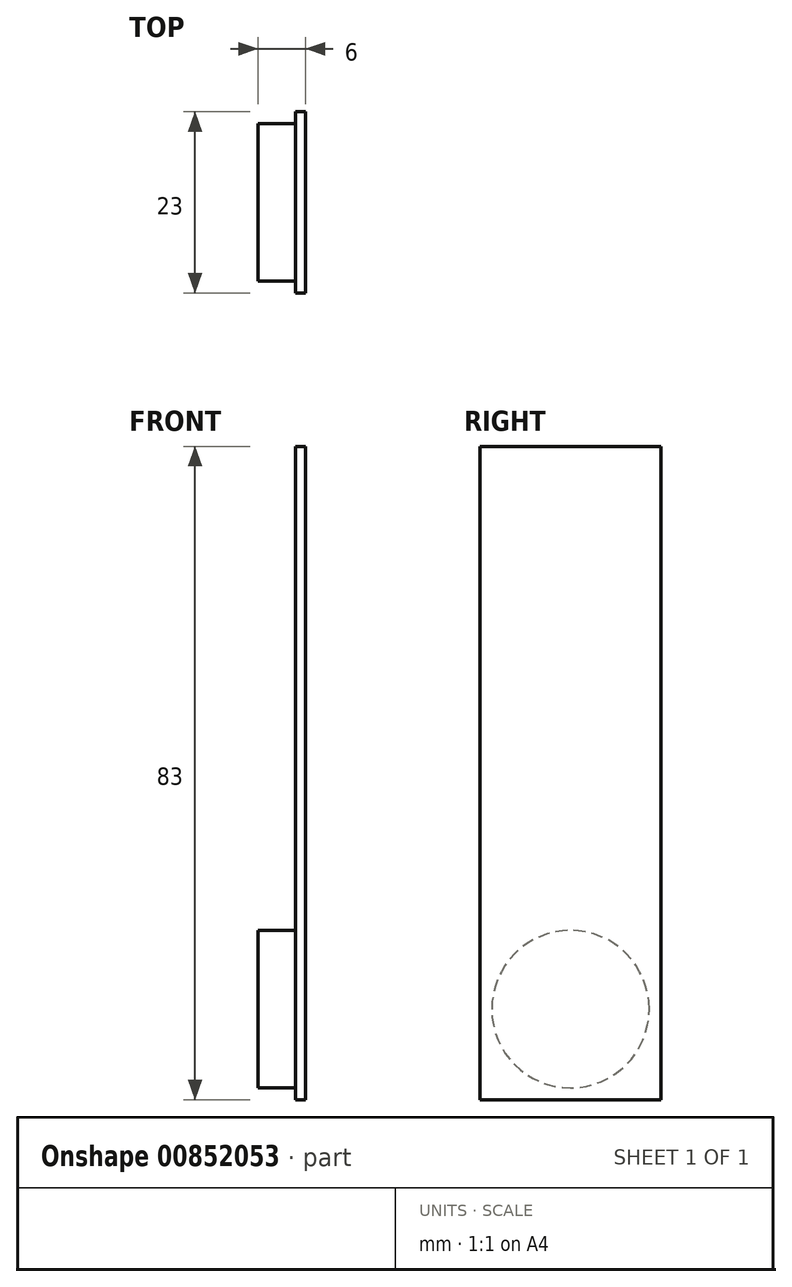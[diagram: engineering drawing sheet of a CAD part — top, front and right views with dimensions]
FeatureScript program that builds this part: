
annotation { "Feature Type Name" : "Feature", "Feature Type Description" : "" }
export const myFeature = defineFeature(function(context is Context, id is Id, definition is map)
    precondition{}
    {
        {
            var Q0;
            Q0=qCreatedBy(makeId("Top.planeOp"),FACE);
            var sketch = newSketch(context, id + "F0", { "sketchPlane" : qUnion([Q0])});
            skLineSegment(sketch, "E0.bottom", {"start": v(-9.84, -11.5) * mm, "end": v(-3.84, -11.5) * mm});
            skLineSegment(sketch, "E0.top", {"start": v(-9.84, 11.5) * mm, "end": v(-3.84, 11.5) * mm});
            skLineSegment(sketch, "E0.left", {"start": v(-9.84, -11.5) * mm, "end": v(-9.84, 11.5) * mm});
            skLineSegment(sketch, "E0.right", {"start": v(-3.84, -11.5) * mm, "end": v(-3.84, 11.5) * mm});
            skSolve(sketch);
        }
        {
            var Q0;
            Q0 = qSketchRegion(id + "F0", true);
            extrude(context, id + "F1", {"entities" : qUnion([Q0]), "flatOperationType" : FlatOperationType.REMOVE, "depth" : 83 * mm, "offsetDistance" : 25 * mm, "domain" : OperationDomain.MODEL, "symmetric" : true});
        }
        {
            var Q0;
            Q0=makeQuery(id+"F1.opExtrude","SWEPT_FACE",FACE,{"disambiguationData":[OSD([sQuery(id+"F0.wireOp",EDGE,"E0.left")])]});
            var sketch = newSketch(context, id + "F2", { "sketchPlane" : qUnion([Q0])});
            skCircle(sketch, "E1", {"center": v(0, 30) * mm, "radius": 10 * mm});
            skCircle(sketch, "E2.MirrorC", {"center": v(0, -30) * mm, "radius": 10 * mm});
            skSolve(sketch);
        }
        {
            var Q0;
            Q0=makeQuery(id+"F2.imprint","IMPRINT",FACE,{"disambiguationData":[TD([[makeQuery(id+"F2.imprint","IMPRINT",EDGE,{"derivedFrom":sQuery(id+"F2.wireOp",EDGE,"E1")}),1.0]])]});
            var Q1;
            Q1=makeQuery(id+"F2.imprint","IMPRINT",FACE,{"disambiguationData":[TD([[makeQuery(id+"F2.imprint","IMPRINT",EDGE,{"derivedFrom":sQuery(id+"F2.wireOp",EDGE,"E2.MirrorC")}),-1.0]])]});
            extrude(context, id + "F3", {"entities" : qUnion([Q0, Q1]), "operationType" : NewBodyOperationType.REMOVE, "flatOperationType" : FlatOperationType.REMOVE, "oppositeDirection" : true, "depth" : 4.75 * mm, "offsetDistance" : 25 * mm, "domain" : OperationDomain.MODEL});
        }
    });
